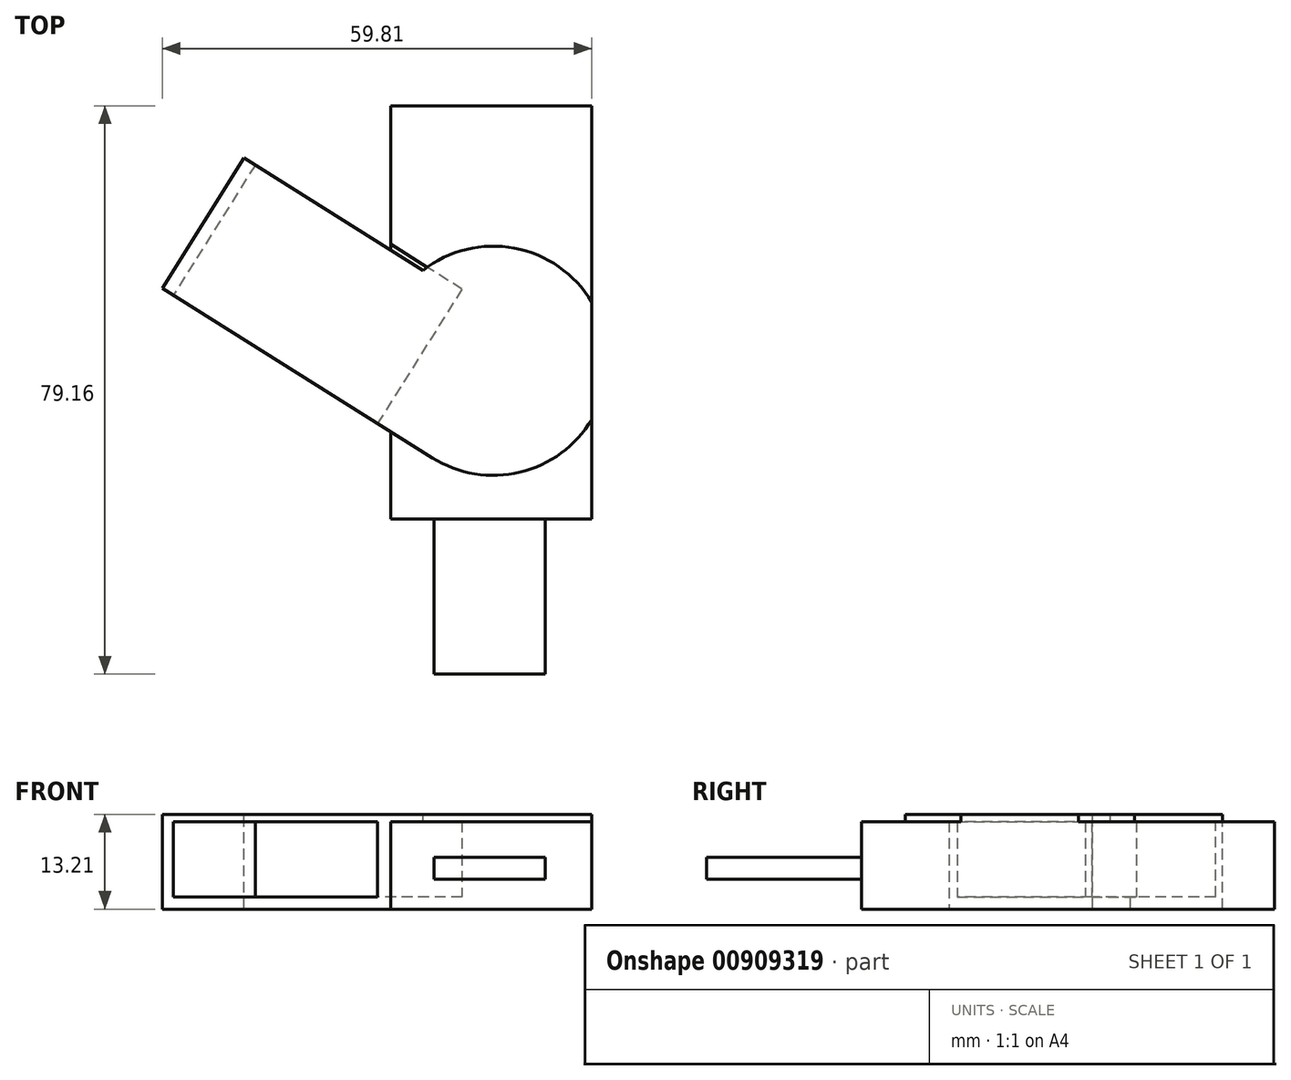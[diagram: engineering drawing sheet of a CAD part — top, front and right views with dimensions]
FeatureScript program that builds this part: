
annotation { "Feature Type Name" : "Feature", "Feature Type Description" : "" }
export const myFeature = defineFeature(function(context is Context, id is Id, definition is map)
    precondition{}
    {
        {
            var Q0;
            Q0=qCreatedBy(makeId("Top.planeOp"),FACE);
            var sketch = newSketch(context, id + "F0", { "sketchPlane" : qUnion([Q0])});
            skLineSegment(sketch, "E0.bottom", {"start": v(-17.9, 41.23) * mm, "end": v(10.11, 41.23) * mm});
            skLineSegment(sketch, "E0.top", {"start": v(-17.9, -16.34) * mm, "end": v(10.11, -16.34) * mm});
            skLineSegment(sketch, "E0.left", {"start": v(-17.9, 41.23) * mm, "end": v(-17.9, -16.34) * mm});
            skLineSegment(sketch, "E0.right", {"start": v(10.11, 41.23) * mm, "end": v(10.11, -16.34) * mm});
            skSolve(sketch);
        }
        {
            var Q0;
            Q0=makeQuery(id+"F0.imprint","IMPRINT",FACE,{"disambiguationData":[TD([[makeQuery(id+"F0.imprint","IMPRINT",EDGE,{"derivedFrom":sQuery(id+"F0.wireOp",EDGE,"E0.bottom")}),-1.0]])]});
            extrude(context, id + "F1", {"entities" : qUnion([Q0]), "depth" : 12.2 * mm, "offsetDistance" : 25.4 * mm});
        }
        {
            var Q0;
            Q0=makeQuery(id+"F1.opExtrude","SWEPT_FACE",FACE,{"disambiguationData":[OSD([sQuery(id+"F0.wireOp",EDGE,"E0.top")])]});
            var sketch = newSketch(context, id + "F2", { "sketchPlane" : qUnion([Q0])});
            skLineSegment(sketch, "E1.bottom", {"start": v(3.65, 7.19) * mm, "end": v(-11.87, 7.19) * mm});
            skLineSegment(sketch, "E1.top", {"start": v(3.65, 4.15) * mm, "end": v(-11.87, 4.15) * mm});
            skLineSegment(sketch, "E1.left", {"start": v(3.65, 7.19) * mm, "end": v(3.65, 4.15) * mm});
            skLineSegment(sketch, "E1.right", {"start": v(-11.87, 7.19) * mm, "end": v(-11.87, 4.15) * mm});
            skSolve(sketch);
        }
        {
            var Q0;
            Q0=makeQuery(id+"F2.imprint","IMPRINT",FACE,{"disambiguationData":[TD([[makeQuery(id+"F2.imprint","IMPRINT",EDGE,{"derivedFrom":sQuery(id+"F2.wireOp",EDGE,"E1.bottom")}),1.0]])]});
            extrude(context, id + "F3", {"entities" : qUnion([Q0]), "operationType" : NewBodyOperationType.ADD, "depth" : 21.59 * mm, "offsetDistance" : 25.4 * mm});
        }
        {
            var Q0;
            Q0=makeQuery(id+"F1.opExtrude","CAP_FACE",FACE,{"disambiguationData":[OSD([sQuery(id+"F0.wireOp",EDGE,"E0.bottom"),sQuery(id+"F0.wireOp",EDGE,"E0.top"),sQuery(id+"F0.wireOp",EDGE,"E0.left"),sQuery(id+"F0.wireOp",EDGE,"E0.right")])],"isStart":false});
            var sketch = newSketch(context, id + "F4", { "sketchPlane" : qUnion([Q0])});
            skCircle(sketch, "E2", {"center": v(-3.6, 5.73) * mm, "radius": 15.96 * mm});
            skSolve(sketch);
        }
        {
            var Q0;
            {var subQ0=sQuery(id+"F4.wireOp",EDGE,"E2");var subQ1=makeQuery(id+"F1.opExtrude","CAP_EDGE",EDGE,{"disambiguationData":[OSD([sQuery(id+"F0.wireOp",EDGE,"E0.left")])],"isStart":false});var subQ2=makeQuery(id+"F4.imprint","INTERSECT",VERTEX,{"disambiguationData":[OD(0.0)],"derivedFrom":[subQ1,subQ0]});Q0=makeQuery(id+"F4.imprint","IMPRINT",FACE,{"disambiguationData":[TD([[makeQuery(id+"F4.imprint","IMPRINT",EDGE,{"disambiguationData":[TD([[subQ2,1.0]])],"derivedFrom":subQ0}),1.0]])]});}
            extrude(context, id + "F5", {"entities" : qUnion([Q0]), "operationType" : NewBodyOperationType.ADD, "depth" : 1.02 * mm, "offsetDistance" : 25.4 * mm});
        }
        {
            var Q0;
            Q0=makeQuery(id+"F5.opExtrude","CAP_FACE",FACE,{"disambiguationData":[OSD([sQuery(id+"F0.wireOp",EDGE,"E0.left"),sQuery(id+"F0.wireOp",EDGE,"E0.right"),sQuery(id+"F4.wireOp",EDGE,"E2")])],"isStart":false});
            var sketch = newSketch(context, id + "F6", { "sketchPlane" : qUnion([Q0])});
            skLineSegment(sketch, "E3", {"start": v(-13.4, 18.32) * mm, "end": v(-38.31, 33.97) * mm});
            skLineSegment(sketch, "E4", {"start": v(-38.31, 33.97) * mm, "end": v(-49.7, 15.84) * mm});
            skLineSegment(sketch, "E5", {"start": v(-49.7, 15.84) * mm, "end": v(-12.09, -7.79) * mm});
            skSolve(sketch);
        }
        {
            var Q0;
            {var subQ3=sQuery(id+"F6.wireOp",EDGE,"E3");Q0=makeQuery(id+"F6.imprint","IMPRINT",FACE,{"disambiguationData":[TD([[makeQuery(id+"F6.imprint","IMPRINT",EDGE,{"derivedFrom":subQ3}),1.0]])]});}
            extrude(context, id + "F7", {"entities" : qUnion([Q0]), "operationType" : NewBodyOperationType.ADD, "oppositeDirection" : true, "depth" : 13.2 * mm, "offsetDistance" : 25.4 * mm});
        }
        {
            var Q0;
            Q0=makeQuery(id+"F7.opExtrude","SWEPT_FACE",FACE,{"disambiguationData":[OSD([sQuery(id+"F6.wireOp",EDGE,"E5")])]});
            var sketch = newSketch(context, id + "F8", { "sketchPlane" : qUnion([Q0])});
            skLineSegment(sketch, "E6.bottom", {"start": v(-15.09, 12.2) * mm, "end": v(-48.69, 12.2) * mm});
            skLineSegment(sketch, "E6.top", {"start": v(-15.09, 1.69) * mm, "end": v(-48.69, 1.69) * mm});
            skLineSegment(sketch, "E6.left", {"start": v(-15.09, 12.2) * mm, "end": v(-15.09, 1.69) * mm});
            skLineSegment(sketch, "E6.right", {"start": v(-48.69, 12.2) * mm, "end": v(-48.69, 1.69) * mm});
            skSolve(sketch);
        }
        {
            var Q0;
            Q0=makeQuery(id+"F8.imprint","IMPRINT",FACE,{"disambiguationData":[TD([[makeQuery(id+"F8.imprint","IMPRINT",EDGE,{"derivedFrom":sQuery(id+"F8.wireOp",EDGE,"E6.bottom")}),1.0]])]});
            extrude(context, id + "F9", {"entities" : qUnion([Q0]), "operationType" : NewBodyOperationType.REMOVE, "oppositeDirection" : true, "depth" : 22.1 * mm, "offsetDistance" : 25.4 * mm});
        }
    });
